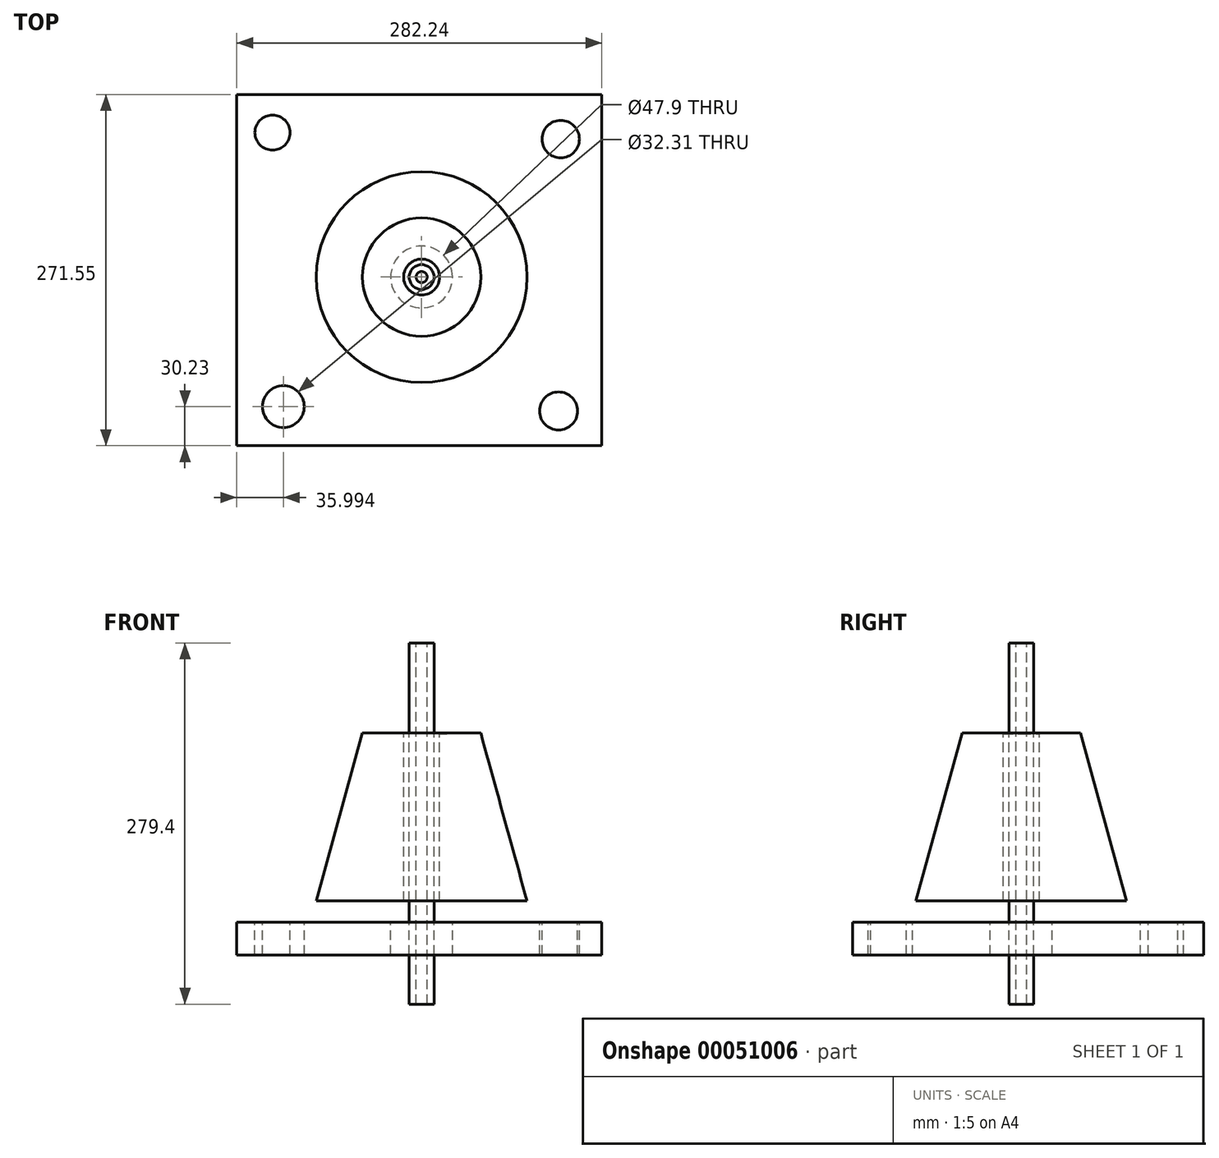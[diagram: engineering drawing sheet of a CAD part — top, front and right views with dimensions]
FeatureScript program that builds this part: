
annotation { "Feature Type Name" : "Feature", "Feature Type Description" : "" }
export const myFeature = defineFeature(function(context is Context, id is Id, definition is map)
    precondition{}
    {
        {
            var Q0;
            Q0=qCreatedBy(makeId("Front.planeOp"),FACE);
            var sketch = newSketch(context, id + "F0", { "sketchPlane" : qUnion([Q0])});
            skLineSegment(sketch, "E0", {"start": v(-45.75, 69.93) * mm, "end": v(-81.47, -59.9) * mm});
            skLineSegment(sketch, "E1", {"start": v(-81.47, -59.9) * mm, "end": v(-13.94, -59.9) * mm});
            skLineSegment(sketch, "E2", {"start": v(-13.94, -59.9) * mm, "end": v(-13.94, 69.5) * mm});
            skLineSegment(sketch, "E3", {"start": v(-13.94, 69.5) * mm, "end": v(-45.75, 69.93) * mm});
            skLineSegment(sketch, "E4", {"start": v(0, 72.98) * mm, "end": v(0, -58.6) * mm});
            skSolve(sketch);
        }
        {
            var Q0;
            Q0=makeQuery(id+"F0.imprint","IMPRINT",FACE,{"disambiguationData":[TD([[makeQuery(id+"F0.imprint","IMPRINT",EDGE,{"derivedFrom":sQuery(id+"F0.wireOp",EDGE,"E0")}),1.0]])]});
            var Q1;
            Q1=sQuery(id+"F0.wireOp",EDGE,"E4");
            revolve(context, id + "F1", {"entities" : qUnion([Q0]), "axis" : qUnion([Q1]), "revolveType" : RevolveType.FULL});
        }
        {
            var Q0;
            Q0=qCreatedBy(makeId("Top.planeOp"),FACE);
            var sketch = newSketch(context, id + "F2", { "sketchPlane" : qUnion([Q0])});
            skCircle(sketch, "E5", {"center": v(0, 0) * mm, "radius": 9.59 * mm});
            skCircle(sketch, "E6", {"center": v(0, 0) * mm, "radius": 4.23 * mm});
            skSolve(sketch);
        }
        {
            var Q0;
            Q0=makeQuery(id+"F2.imprint","IMPRINT",FACE,{"disambiguationData":[TD([[makeQuery(id+"F2.imprint","IMPRINT",EDGE,{"derivedFrom":sQuery(id+"F2.wireOp",EDGE,"E5")}),1.0]])]});
            extrude(context, id + "F3", {"entities" : qUnion([Q0]), "endBound" : BoundingType.SYMMETRIC, "oppositeDirection" : true, "depth" : 279.4 * mm});
        }
        {
            var Q0;
            Q0=qCreatedBy(makeId("Top.planeOp"),FACE);
            cPlane(context, id + "F4", {"entities" : qUnion([Q0]), "cplaneType" : CPlaneType.OFFSET, "offset" : 76.2 * mm, "oppositeDirection" : true, "width" : 152.4 * mm, "height" : 152.4 * mm});
        }
        {
            var Q0;
            Q0=qCreatedBy(id+"F4.planeOp",FACE);
            var sketch = newSketch(context, id + "F5", { "sketchPlane" : qUnion([Q0])});
            skLineSegment(sketch, "E7.bottom", {"start": v(139.34, -130.43) * mm, "end": v(-142.9, -130.43) * mm});
            skLineSegment(sketch, "E7.top", {"start": v(139.34, 141.12) * mm, "end": v(-142.9, 141.12) * mm});
            skLineSegment(sketch, "E7.left", {"start": v(139.34, -130.43) * mm, "end": v(139.34, 141.12) * mm});
            skLineSegment(sketch, "E7.right", {"start": v(-142.9, -130.43) * mm, "end": v(-142.9, 141.12) * mm});
            skCircle(sketch, "E8", {"center": v(0, 0) * mm, "radius": 23.95 * mm});
            skCircle(sketch, "E9", {"center": v(-115.32, 111.73) * mm, "radius": 13.59 * mm});
            skCircle(sketch, "E10", {"center": v(107.55, 106.69) * mm, "radius": 14.47 * mm});
            skCircle(sketch, "E11", {"center": v(105.87, -103.56) * mm, "radius": 14.69 * mm});
            skCircle(sketch, "E12", {"center": v(-106.9, -100.2) * mm, "radius": 16.16 * mm});
            skSolve(sketch);
        }
        {
            var Q0;
            Q0=makeQuery(id+"F5.imprint","IMPRINT",FACE,{"disambiguationData":[TD([[makeQuery(id+"F5.imprint","IMPRINT",EDGE,{"derivedFrom":sQuery(id+"F5.wireOp",EDGE,"E7.bottom")}),-1.0]])]});
            extrude(context, id + "F6", {"entities" : qUnion([Q0]), "oppositeDirection" : true, "depth" : 25.4 * mm});
        }
    });
